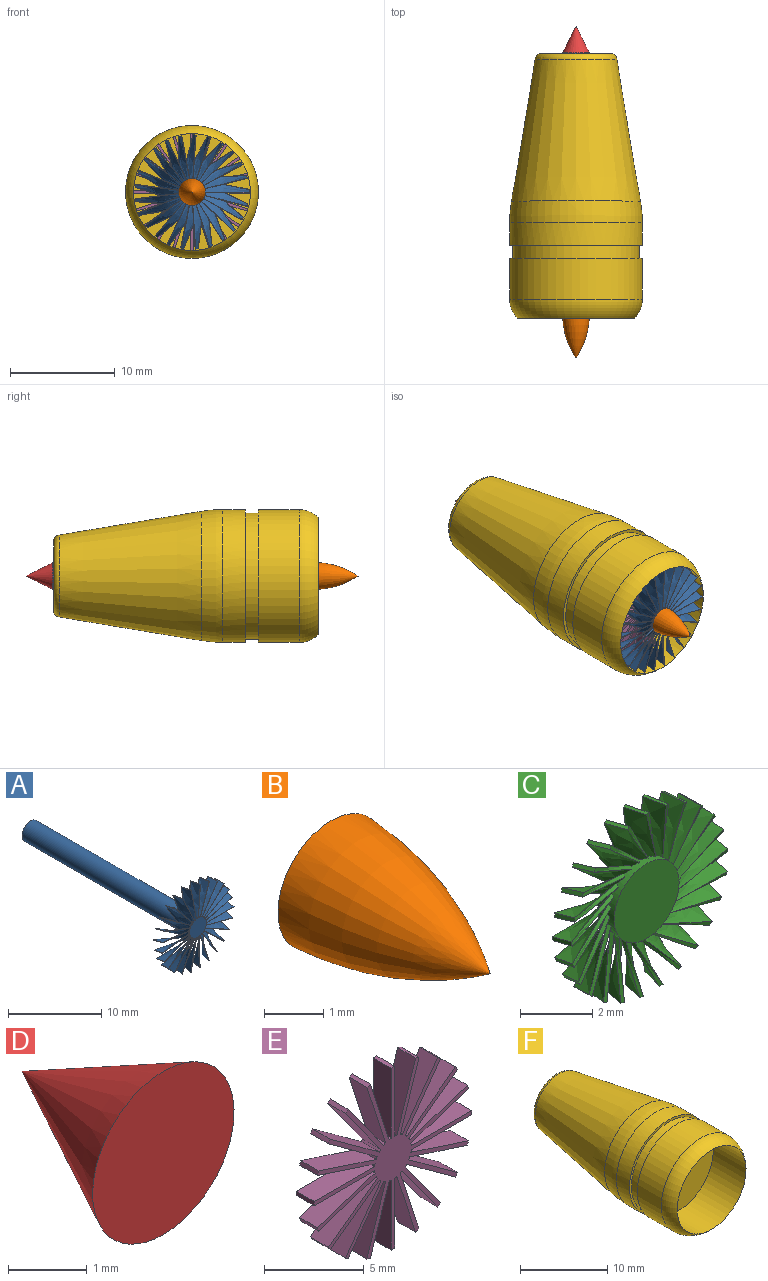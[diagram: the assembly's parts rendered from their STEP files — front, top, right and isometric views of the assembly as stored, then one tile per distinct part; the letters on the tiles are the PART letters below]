
ASSEMBLY  parts=6 mates=5
PART A: 155 faces, bbox 10.9x25.4x10.9 mm
  f0: cylinder r=1.27mm len=25.4mm, axis (0,-1,0), area 201.4mm2, adj f1,f2,f3,f4,f5,f7,f8,f9
  f1: cylinder r=1.27mm len=0.24mm, axis (0,-1,0), area 0mm2, adj f0,f4,f63
  f2: cylinder r=1.27mm len=0.54mm, axis (0,-1,0), area 0.1mm2, adj f0,f4,f57,f61,f62
  f3: plane 2.54x2.54mm, normal (0,1,0), area 5.1mm2, adj f0
  f4: plane 2.54x2.54mm, normal (0,-1,0), area 5.1mm2, adj f0,f1,f2
  f5: plane 0.37x0.23mm, normal (-1,0,0), area 0mm2, adj f0,f7,f9,f10
  f6: plane 1.26x0.3mm, normal (1,0,0), area 0.1mm2, adj f7,f8,f9,f10
  f7: bspline ~4.45x1.25mm, area 5.2mm2, adj f0,f5,f6,f8,f10
  f8: bspline ~4.45x0.05mm, area 0.2mm2, adj f0,f6,f7,f9
  f9: bspline ~4.45x1.25mm, area 5.2mm2, adj f0,f5,f6,f8,f10
  f10: bspline ~4.45x0.94mm, area 0.2mm2, adj f5,f6,f7,f9
  f11: plane 1.26x0.26mm, normal (0.88,0,0.48), area 0.1mm2, adj f12,f13,f14,f15
  f12: bspline ~4.35x1.38mm, area 0.2mm2, adj f11,f13,f15,f16
  f13: bspline ~4.46x2.34mm, area 5.2mm2, adj f0,f11,f12,f14,f16
  f14: bspline ~3.92x2.16mm, area 0.2mm2, adj f0,f11,f13,f15
  f15: bspline ~4.44x2.36mm, area 5.2mm2, adj f0,f11,f12,f14,f16
  f16: plane 0.33x0.23mm, normal (-0.88,0,-0.48), area 0mm2, adj f0,f12,f13,f15
  f17: plane 1.26x0.22mm, normal (0.73,0,0.68), area 0.1mm2, adj f18,f19,f20,f21
  f18: bspline ~3.88x2.41mm, area 0.2mm2, adj f17,f19,f21,f22
  f19: bspline ~4.04x3.2mm, area 5.2mm2, adj f0,f17,f18,f20,f22
  f20: bspline ~3.09x2.89mm, area 0.2mm2, adj f0,f17,f19,f21
  f21: bspline ~4.02x3.22mm, area 5.2mm2, adj f0,f17,f18,f20,f22
  f22: plane 0.27x0.26mm, normal (-0.73,0,-0.68), area 0mm2, adj f0,f18,f19,f21
  f23: plane 1.26x0.3mm, normal (0.06,0,1), area 0.1mm2, adj f24,f25,f26,f27
  f24: bspline ~4.38x1.21mm, area 0.2mm2, adj f23,f25,f27,f28
  f25: bspline ~4.45x1.44mm, area 5.2mm2, adj f0,f23,f24,f26,f28
  f26: bspline ~4.44x0.33mm, area 0.2mm2, adj f0,f23,f25,f27
  f27: bspline ~4.45x1.41mm, area 5.2mm2, adj f0,f23,f24,f26,f28
  f28: plane 0.37x0.23mm, normal (-0.06,0,-1), area 0mm2, adj f0,f24,f25,f27
  f29: plane 1.26x0.27mm, normal (-0.43,0,0.9), area 0.1mm2, adj f30,f31,f32,f33
  f30: bspline ~4.42x1.11mm, area 0.2mm2, adj f29,f31,f33,f34
  f31: bspline ~4.52x2.09mm, area 5.2mm2, adj f0,f29,f30,f32,f34
  f32: bspline ~4.04x1.91mm, area 0.2mm2, adj f0,f29,f31,f33
  f33: bspline ~4.51x2.12mm, area 5.2mm2, adj f0,f29,f30,f32,f34
  f34: plane 0.34x0.23mm, normal (0.43,0,-0.9), area 0mm2, adj f0,f30,f31,f33
  f35: plane 1.26x0.24mm, normal (-0.81,0,0.59), area 0.1mm2, adj f36,f37,f38,f39
  f36: bspline ~3.37x3.09mm, area 0.2mm2, adj f35,f37,f39,f40
  f37: bspline ~3.73x3.55mm, area 5.2mm2, adj f0,f35,f36,f38,f40
  f38: bspline ~3.61x2.65mm, area 0.2mm2, adj f0,f35,f37,f39
  f39: bspline ~3.74x3.53mm, area 5.2mm2, adj f0,f35,f36,f38,f40
  f40: plane 0.3x0.23mm, normal (0.81,0,-0.59), area 0mm2, adj f0,f36,f37,f39
  f41: plane 1.26x0.3mm, normal (-0.99,0,0.13), area 0.1mm2, adj f42,f43,f44,f45
  f42: bspline ~4.3x1.49mm, area 0.2mm2, adj f41,f43,f45,f46
  f43: bspline ~4.44x1.71mm, area 5.2mm2, adj f0,f41,f42,f44,f46
  f44: bspline ~4.16x0.57mm, area 0.2mm2, adj f0,f41,f43,f45
  f45: bspline ~4.44x1.68mm, area 5.2mm2, adj f0,f41,f42,f44,f46
  f46: plane 0.37x0.23mm, normal (0.99,0,-0.13), area 0mm2, adj f0,f42,f43,f45
  f47: plane 1.26x0.28mm, normal (-0.93,0,-0.37), area 0.1mm2, adj f48,f49,f50,f51
  f48: bspline ~4.48x0.83mm, area 0.2mm2, adj f47,f49,f51,f52
  f49: bspline ~4.56x1.84mm, area 5.2mm2, adj f0,f47,f48,f50,f52
  f50: bspline ~4.15x1.66mm, area 0.2mm2, adj f0,f47,f49,f51
  f51: bspline ~4.55x1.87mm, area 5.2mm2, adj f0,f47,f48,f50,f52
  f52: plane 0.35x0.23mm, normal (0.93,0,0.37), area 0mm2, adj f0,f48,f49,f51
  f53: plane 1.26x0.27mm, normal (-0.43,0,-0.9), area 0.1mm2, adj f54,f55,f56,f57
  f54: bspline ~3.65x2.74mm, area 0.2mm2, adj f53,f55,f57,f58
  f55: bspline ~4.12x2.95mm, area 5.2mm2, adj f0,f53,f54,f56,f58
  f56: bspline ~4.03x1.94mm, area 0.2mm2, adj f0,f53,f55,f57
  f57: bspline ~4.13x2.92mm, area 5.2mm2, adj f0,f2,f53,f54,f56,f58
  f58: plane 0.34x0.23mm, normal (0.43,0,0.9), area 0mm2, adj f0,f54,f55,f57
  f59: plane 1.26x0.29mm, normal (-0.19,0,-0.98), area 0.1mm2, adj f60,f61,f62,f63
  f60: bspline ~4.2x1.75mm, area 0.2mm2, adj f59,f61,f63,f64
  f61: bspline ~4.41x1.98mm, area 5.2mm2, adj f0,f2,f59,f60,f62,f64
  f62: bspline ~4.37x0.88mm, area 0.2mm2, adj f2,f59,f61,f63
  f63: bspline ~4.41x1.95mm, area 5.2mm2, adj f0,f1,f59,f60,f62,f64
  f64: plane 0.37x0.23mm, normal (0.19,0,0.98), area 0mm2, adj f0,f60,f61,f63
  f65: plane 1.26x0.28mm, normal (0.31,0,-0.95), area 0.1mm2, adj f66,f67,f68,f69
  f66: bspline ~4.52x0.69mm, area 0.2mm2, adj f65,f67,f69,f70
  f67: bspline ~4.59x1.58mm, area 5.2mm2, adj f0,f65,f66,f68,f70
  f68: bspline ~4.24x1.4mm, area 0.2mm2, adj f0,f65,f67,f69
  f69: bspline ~4.58x1.61mm, area 5.2mm2, adj f0,f65,f66,f68,f70
  f70: plane 0.36x0.23mm, normal (-0.31,0,0.95), area 0mm2, adj f0,f66,f67,f69
  f71: plane 1.26x0.22mm, normal (0.73,0,-0.68), area 0.1mm2, adj f72,f73,f74,f75
  f72: bspline ~3.73x2.65mm, area 0.2mm2, adj f71,f73,f75,f76
  f73: bspline ~3.89x3.39mm, area 5.2mm2, adj f0,f71,f72,f74,f76
  f74: bspline ~3.26x3.08mm, area 0.2mm2, adj f0,f71,f73,f75
  f75: bspline ~3.87x3.41mm, area 5.2mm2, adj f0,f71,f72,f74,f76
  f76: plane 0.27x0.26mm, normal (-0.73,0,0.68), area 0mm2, adj f0,f72,f73,f75
  f77: plane 1.26x0.29mm, normal (0.97,0,-0.25), area 0.1mm2, adj f78,f79,f80,f81
  f78: bspline ~4.09x2.01mm, area 0.2mm2, adj f77,f79,f81,f82
  f79: bspline ~4.36x2.23mm, area 5.2mm2, adj f0,f77,f78,f80,f82
  f80: bspline ~4.07x1.09mm, area 0.2mm2, adj f0,f77,f79,f81
  f81: bspline ~4.37x2.21mm, area 5.2mm2, adj f0,f77,f78,f80,f82
  f82: plane 0.36x0.23mm, normal (-0.97,0,0.25), area 0mm2, adj f0,f78,f79,f81
  f83: plane 1.26x0.26mm, normal (0.88,0,-0.48), area 0.1mm2, adj f84,f86,f87,f88
  f84: bspline ~3.48x2.96mm, area 0.2mm2, adj f83,f85,f86,f88
  f85: plane 0.33x0.23mm, normal (-0.88,0,0.48), area 0mm2, adj f0,f84,f86,f88
  f86: bspline ~4.02x3.14mm, area 5.2mm2, adj f0,f83,f84,f85,f87
  f87: bspline ~3.91x2.19mm, area 0.2mm2, adj f0,f83,f86,f88
  f88: bspline ~4x3.16mm, area 5.2mm2, adj f0,f83,f84,f85,f87
  f89: plane 1.26x0.25mm, normal (0.54,0,-0.84), area 0.1mm2, adj f90,f92,f93,f94
  f90: bspline ~4.26x1.65mm, area 0.2mm2, adj f89,f91,f92,f94
  f91: plane 0.32x0.23mm, normal (-0.54,0,0.84), area 0mm2, adj f0,f90,f92,f94
  f92: bspline ~4.36x2.59mm, area 5.2mm2, adj f0,f89,f90,f91,f93
  f93: bspline ~3.57x2.27mm, area 0.2mm2, adj f0,f89,f92,f94
  f94: bspline ~4.38x2.57mm, area 5.2mm2, adj f0,f89,f90,f91,f93
  f95: plane 1.26x0.3mm, normal (0.06,0,-1), area 0.1mm2, adj f96,f98,f99,f100
  f96: bspline ~4.5x0.69mm, area 0.2mm2, adj f95,f97,f98,f100
  f97: plane 0.37x0.23mm, normal (-0.06,0,1), area 0mm2, adj f0,f96,f98,f100
  f98: bspline ~4.51x1.25mm, area 5.2mm2, adj f0,f95,f96,f97,f99
  f99: bspline ~4.44x0.3mm, area 0.2mm2, adj f0,f95,f98,f100
  f100: bspline ~4.51x1.25mm, area 5.2mm2, adj f0,f95,f96,f97,f99
  f101: plane 1.26x0.23mm, normal (-0.64,0,-0.77), area 0.1mm2, adj f102,f104,f105,f106
  f102: bspline ~3.56x2.87mm, area 0.2mm2, adj f101,f103,f104,f106
  f103: plane 0.29x0.24mm, normal (0.64,0,0.77), area 0mm2, adj f0,f102,f104,f106
  f104: bspline ~3.71x3.58mm, area 5.2mm2, adj f0,f101,f102,f103,f105
  f105: bspline ~3.25x2.71mm, area 0.2mm2, adj f0,f101,f104,f106
  f106: bspline ~3.73x3.57mm, area 5.2mm2, adj f0,f101,f102,f103,f105
  f107: plane 1.26x0.24mm, normal (-0.81,0,-0.59), area 0.1mm2, adj f108,f110,f111,f112
  f108: bspline ~4.15x1.91mm, area 0.2mm2, adj f107,f109,f110,f112
  f109: plane 0.3x0.23mm, normal (0.81,0,0.59), area 0mm2, adj f0,f108,f110,f112
  f110: bspline ~4.26x2.81mm, area 5.2mm2, adj f0,f107,f108,f109,f111
  f111: bspline ~3.42x2.48mm, area 0.2mm2, adj f0,f107,f110,f112
  f112: bspline ~4.28x2.79mm, area 5.2mm2, adj f0,f107,f108,f109,f111
  f113: plane 1.26x0.3mm, normal (-0.99,0,-0.13), area 0.1mm2, adj f114,f116,f117,f118
  f114: bspline ~4.53x0.69mm, area 0.2mm2, adj f113,f115,f116,f118
  f115: plane 0.37x0.23mm, normal (0.99,0,0.13), area 0mm2, adj f0,f114,f116,f118
  f116: bspline ~4.55x1.25mm, area 5.2mm2, adj f0,f113,f114,f115,f117
  f117: bspline ~4.42x0.58mm, area 0.2mm2, adj f0,f113,f116,f118
  f118: bspline ~4.56x1.25mm, area 5.2mm2, adj f0,f113,f114,f115,f117
  f119: plane 1.26x0.28mm, normal (-0.93,0,0.37), area 0.1mm2, adj f120,f122,f123,f124
  f120: bspline ~3.81x2.51mm, area 0.2mm2, adj f119,f121,f122,f124
  f121: plane 0.35x0.23mm, normal (0.93,0,-0.37), area 0mm2, adj f0,f120,f122,f124
  f122: bspline ~4.22x2.69mm, area 5.2mm2, adj f0,f119,f120,f121,f123
  f123: bspline ~3.91x1.59mm, area 0.2mm2, adj f0,f119,f122,f124
  f124: bspline ~4.21x2.72mm, area 5.2mm2, adj f0,f119,f120,f121,f123
  f125: plane 1.26x0.23mm, normal (-0.64,0,0.77), area 0.1mm2, adj f126,f128,f129,f130
  f126: bspline ~4.02x2.17mm, area 0.2mm2, adj f125,f127,f128,f130
  f127: plane 0.29x0.24mm, normal (0.64,0,-0.77), area 0mm2, adj f0,f126,f128,f130
  f128: bspline ~4.15x3.03mm, area 5.2mm2, adj f0,f125,f126,f127,f129
  f129: bspline ~3.46x2.85mm, area 0.2mm2, adj f0,f125,f128,f130
  f130: bspline ~4.17x3mm, area 5.2mm2, adj f0,f125,f126,f127,f129
  f131: plane 1.26x0.29mm, normal (-0.19,0,0.98), area 0.1mm2, adj f132,f134,f135,f136
  f132: bspline ~4.54x0.69mm, area 0.2mm2, adj f131,f133,f134,f136
  f133: plane 0.37x0.23mm, normal (0.19,0,-0.98), area 0mm2, adj f0,f132,f134,f136
  f134: bspline ~4.58x1.25mm, area 5.2mm2, adj f0,f131,f132,f133,f135
  f135: bspline ~4.13x0.81mm, area 0.2mm2, adj f0,f131,f134,f136
  f136: bspline ~4.58x1.25mm, area 5.2mm2, adj f0,f131,f132,f133,f135
  f137: plane 1.26x0.28mm, normal (0.31,0,0.95), area 0.1mm2, adj f138,f140,f141,f142
  f138: bspline ~3.96x2.26mm, area 0.2mm2, adj f137,f139,f140,f142
  f139: plane 0.36x0.23mm, normal (-0.31,0,-0.95), area 0mm2, adj f0,f138,f140,f142
  f140: bspline ~4.3x2.45mm, area 5.2mm2, adj f0,f137,f138,f139,f141
  f141: bspline ~4.23x1.42mm, area 0.2mm2, adj f0,f137,f140,f142
  f142: bspline ~4.3x2.48mm, area 5.2mm2, adj f0,f137,f138,f139,f141
  f143: plane 1.26x0.25mm, normal (0.54,0,0.84), area 0.1mm2, adj f144,f146,f147,f148
  f144: bspline ~3.29x3.17mm, area 0.2mm2, adj f143,f145,f146,f148
  f145: plane 0.32x0.23mm, normal (-0.54,0,-0.84), area 0mm2, adj f0,f144,f146,f148
  f146: bspline ~3.89x3.34mm, area 5.2mm2, adj f0,f143,f144,f145,f147
  f147: bspline ~3.55x2.29mm, area 0.2mm2, adj f0,f143,f146,f148
  f148: bspline ~3.87x3.36mm, area 5.2mm2, adj f0,f143,f144,f145,f147
  f149: plane 0.36x0.23mm, normal (-0.97,0,-0.25), area 0mm2, adj f0,f151,f153,f154
  f150: plane 1.26x0.29mm, normal (0.97,0,0.25), area 0.1mm2, adj f151,f152,f153,f154
  f151: bspline ~4.59x1.35mm, area 5.2mm2, adj f0,f149,f150,f152,f154
  f152: bspline ~4.32x1.13mm, area 0.2mm2, adj f0,f150,f151,f153
  f153: bspline ~4.59x1.32mm, area 5.2mm2, adj f0,f149,f150,f152,f154
  f154: bspline ~4.54x0.69mm, area 0.2mm2, adj f149,f150,f151,f153
PART B: 2 faces, bbox 2.5x3.8x2.5 mm
  f0: plane 2.54x2.54mm, normal (0,1,0), area 5.1mm2, adj f1
  f1: revolved ~3.81x2.54mm, area 20.7mm2, adj f0
PART C: 153 faces, bbox 6.1x0.8x6.1 mm
  f0: bspline ~2.03x0.12mm, area 0.2mm2, adj f1,f2,f3,f146
  f1: bspline ~2.03x0.75mm, area 1.3mm2, adj f0,f2,f4,f10,f11,f126,f146
  f2: plane 0.77x0.31mm, normal (-1,0,0), area 0.1mm2, adj f0,f1,f3,f4
  f3: bspline ~2.03x0.74mm, area 1.3mm2, adj f0,f2,f4,f6,f149
  f4: bspline ~2.03x0.62mm, area 0.2mm2, adj f1,f2,f3,f6,f126
  f5: bspline ~1.75x0.51mm, area 0.2mm2, adj f6,f122,f123,f149
  f6: bspline ~2.04x0.74mm, area 1.3mm2, adj f3,f4,f5,f122,f124,f126,f149
  f7: bspline ~1.98x0.62mm, area 0.2mm2, adj f8,f9,f10,f143
  f8: bspline ~2x1.23mm, area 1.3mm2, adj f7,f9,f11,f15,f16,f126,f143
  f9: plane 0.77x0.3mm, normal (-0.97,0,-0.25), area 0.1mm2, adj f7,f8,f10,f11
  f10: bspline ~1.92x1.12mm, area 1.3mm2, adj f1,f7,f9,f11,f146
  f11: bspline ~1.86x1.11mm, area 0.2mm2, adj f1,f8,f9,f10,f126
  f12: bspline ~1.81x1.09mm, area 0.2mm2, adj f13,f14,f15,f140
  f13: bspline ~1.84x1.63mm, area 1.3mm2, adj f12,f14,f16,f20,f21,f126,f140
  f14: plane 0.77x0.27mm, normal (-0.88,0,-0.48), area 0.1mm2, adj f12,f13,f15,f16
  f15: bspline ~1.87x1.58mm, area 1.3mm2, adj f8,f12,f14,f16,f143
  f16: bspline ~1.57x1.52mm, area 0.2mm2, adj f8,f13,f14,f15,f126
  f17: bspline ~1.34x1.31mm, area 0.2mm2, adj f18,f19,f20,f137
  f18: bspline ~1.94x1.56mm, area 1.3mm2, adj f17,f19,f21,f25,f26,f126,f137
  f19: plane 0.77x0.22mm, normal (-0.73,0,-0.68), area 0.1mm2, adj f17,f18,f20,f21
  f20: bspline ~1.89x1.61mm, area 1.3mm2, adj f13,f17,f19,f21,f140
  f21: bspline ~1.78x1.14mm, area 0.2mm2, adj f13,f18,f19,f20,f126
  f22: bspline ~1.78x1.14mm, area 0.2mm2, adj f23,f24,f25,f134
  f23: bspline ~2.12x1.19mm, area 1.3mm2, adj f22,f24,f26,f30,f31,f126,f134
  f24: plane 0.77x0.26mm, normal (-0.54,0,-0.84), area 0.1mm2, adj f22,f23,f25,f26
  f25: bspline ~2.08x1.25mm, area 1.3mm2, adj f18,f22,f24,f26,f137
  f26: bspline ~2.05x0.72mm, area 0.2mm2, adj f18,f23,f24,f25,f126
  f27: bspline ~1.97x0.68mm, area 0.2mm2, adj f28,f29,f30,f131
  f28: bspline ~2.16x0.74mm, area 1.3mm2, adj f27,f29,f31,f35,f36,f126,f131
  f29: plane 0.77x0.29mm, normal (-0.31,0,-0.95), area 0.1mm2, adj f27,f28,f30,f31
  f30: bspline ~2.14x0.8mm, area 1.3mm2, adj f23,f27,f29,f31,f134
  f31: bspline ~2.12x0.43mm, area 0.2mm2, adj f23,f28,f29,f30,f126
  f32: bspline ~1.78x0.18mm, area 0.2mm2, adj f33,f34,f35,f128
  f33: bspline ~1.97x0.74mm, area 1.3mm2, adj f32,f34,f36,f40,f41,f126,f128
  f34: plane 0.77x0.31mm, normal (-0.06,0,-1), area 0.1mm2, adj f32,f33,f35,f36
  f35: bspline ~2.07x0.74mm, area 1.3mm2, adj f28,f32,f34,f36,f131
  f36: bspline ~2.07x0.49mm, area 0.2mm2, adj f28,f33,f34,f35,f126
  f37: bspline ~2.01x0.5mm, area 0.2mm2, adj f38,f39,f40,f127
  f38: bspline ~2.02x1.12mm, area 1.3mm2, adj f37,f39,f41,f45,f46,f126,f127
  f39: plane 0.77x0.3mm, normal (0.19,0,-0.98), area 0.1mm2, adj f37,f38,f40,f41
  f40: bspline ~2.03x1.05mm, area 1.3mm2, adj f33,f37,f39,f41,f128
  f41: bspline ~1.91x0.99mm, area 0.2mm2, adj f33,f38,f39,f40,f126
  f42: bspline ~1.86x0.98mm, area 0.2mm2, adj f43,f44,f45,f129
  f43: bspline ~1.89x1.54mm, area 1.3mm2, adj f42,f44,f46,f50,f51,f126,f129
  f44: plane 0.77x0.28mm, normal (0.43,0,-0.9), area 0.1mm2, adj f42,f43,f45,f46
  f45: bspline ~1.92x1.48mm, area 1.3mm2, adj f38,f42,f44,f46,f127
  f46: bspline ~1.65x1.43mm, area 0.2mm2, adj f38,f43,f44,f45,f126
  f47: bspline ~1.6x1.39mm, area 0.2mm2, adj f48,f49,f50,f130
  f48: bspline ~1.87x1.64mm, area 1.3mm2, adj f47,f49,f51,f55,f56,f126,f130
  f49: plane 0.77x0.24mm, normal (0.64,0,-0.77), area 0.1mm2, adj f47,f48,f50,f51
  f50: bspline ~1.82x1.68mm, area 1.3mm2, adj f43,f47,f49,f51,f129
  f51: bspline ~1.77x1.29mm, area 0.2mm2, adj f43,f48,f49,f50,f126
  f52: bspline ~1.51x1.1mm, area 0.2mm2, adj f53,f54,f55,f132
  f53: bspline ~2.08x1.29mm, area 1.3mm2, adj f52,f54,f56,f60,f61,f126,f132
  f54: plane 0.77x0.25mm, normal (0.81,0,-0.59), area 0.1mm2, adj f52,f53,f55,f56
  f55: bspline ~1.95x1.29mm, area 1.3mm2, adj f48,f52,f54,f56,f130
  f56: bspline ~2.01x0.84mm, area 0.2mm2, adj f48,f53,f54,f55,f126
  f57: bspline ~1.93x0.8mm, area 0.2mm2, adj f58,f59,f60,f133
  f58: bspline ~2.16x0.86mm, area 1.3mm2, adj f57,f59,f61,f65,f66,f126,f133
  f59: plane 0.77x0.29mm, normal (0.93,0,-0.37), area 0.1mm2, adj f57,f58,f60,f61
  f60: bspline ~2.14x0.92mm, area 1.3mm2, adj f53,f57,f59,f61,f132
  f61: bspline ~2.12x0.43mm, area 0.2mm2, adj f53,f58,f59,f60,f126
  f62: bspline ~2.03x0.31mm, area 0.2mm2, adj f63,f64,f65,f135
  f63: bspline ~2.11x0.74mm, area 1.3mm2, adj f62,f64,f66,f70,f71,f126,f135
  f64: plane 0.77x0.31mm, normal (0.99,0,-0.13), area 0.1mm2, adj f62,f63,f65,f66
  f65: bspline ~2.1x0.74mm, area 1.3mm2, adj f58,f62,f64,f66,f133
  f66: bspline ~2.09x0.43mm, area 0.2mm2, adj f58,f63,f64,f65,f126
  f67: bspline ~2.02x0.38mm, area 0.2mm2, adj f68,f69,f70,f136
  f68: bspline ~2.03x1mm, area 1.3mm2, adj f67,f69,f71,f75,f76,f126,f136
  f69: plane 0.77x0.31mm, normal (0.99,0,0.13), area 0.1mm2, adj f67,f68,f70,f71
  f70: bspline ~2.04x0.93mm, area 1.3mm2, adj f63,f67,f69,f71,f135
  f71: bspline ~1.96x0.87mm, area 0.2mm2, adj f63,f68,f69,f70,f126
  f72: bspline ~1.91x0.86mm, area 0.2mm2, adj f73,f74,f75,f138
  f73: bspline ~1.93x1.44mm, area 1.3mm2, adj f72,f74,f76,f80,f81,f126,f138
  f74: plane 0.77x0.29mm, normal (0.93,0,0.37), area 0.1mm2, adj f72,f73,f75,f76
  f75: bspline ~1.86x1.32mm, area 1.3mm2, adj f68,f72,f74,f76,f136
  f76: bspline ~1.67x1.28mm, area 0.2mm2, adj f68,f73,f74,f75,f126
  f77: bspline ~1.68x1.29mm, area 0.2mm2, adj f78,f79,f80,f139
  f78: bspline ~1.8x1.71mm, area 1.3mm2, adj f77,f79,f81,f85,f86,f126,f139
  f79: plane 0.77x0.25mm, normal (0.81,0,0.59), area 0.1mm2, adj f77,f78,f80,f81
  f80: bspline ~1.75x1.75mm, area 1.3mm2, adj f73,f77,f79,f81,f138
  f81: bspline ~1.7x1.39mm, area 0.2mm2, adj f73,f78,f79,f80,f126
  f82: bspline ~1.45x1.18mm, area 0.2mm2, adj f83,f84,f85,f141
  f83: bspline ~2.04x1.39mm, area 1.3mm2, adj f82,f84,f86,f90,f91,f126,f141
  f84: plane 0.77x0.24mm, normal (0.64,0,0.77), area 0.1mm2, adj f82,f83,f85,f86
  f85: bspline ~2x1.44mm, area 1.3mm2, adj f78,f82,f84,f86,f139
  f86: bspline ~1.96x0.96mm, area 0.2mm2, adj f78,f83,f84,f85,f126
  f87: bspline ~1.66x0.82mm, area 0.2mm2, adj f88,f89,f90,f142
  f88: bspline ~2.05x0.93mm, area 1.3mm2, adj f87,f89,f91,f95,f96,f126,f142
  f89: plane 0.77x0.28mm, normal (0.43,0,0.9), area 0.1mm2, adj f87,f88,f90,f91
  f90: bspline ~2.13x1.03mm, area 1.3mm2, adj f83,f87,f89,f91,f141
  f91: bspline ~2.1x0.47mm, area 0.2mm2, adj f83,f88,f89,f90,f126
  f92: bspline ~2.02x0.44mm, area 0.2mm2, adj f93,f94,f95,f144
  f93: bspline ~2.14x0.74mm, area 1.3mm2, adj f92,f94,f96,f100,f101,f126,f144
  f94: plane 0.77x0.3mm, normal (0.19,0,0.98), area 0.1mm2, adj f92,f93,f95,f96
  f95: bspline ~2.12x0.74mm, area 1.3mm2, adj f88,f92,f94,f96,f142
  f96: bspline ~2.04x0.42mm, area 0.2mm2, adj f88,f93,f94,f95,f126
  f97: bspline ~2.03x0.25mm, area 0.2mm2, adj f98,f99,f100,f145
  f98: bspline ~2.04x0.87mm, area 1.3mm2, adj f97,f99,f101,f105,f106,f126,f145
  f99: plane 0.77x0.31mm, normal (-0.06,0,1), area 0.1mm2, adj f97,f98,f100,f101
  f100: bspline ~1.94x0.78mm, area 1.3mm2, adj f93,f97,f99,f101,f144
  f101: bspline ~2x0.75mm, area 0.2mm2, adj f93,f98,f99,f100,f126
  f102: bspline ~1.71x0.67mm, area 0.2mm2, adj f103,f104,f105,f147
  f103: bspline ~1.97x1.34mm, area 1.3mm2, adj f102,f104,f106,f110,f111,f126,f147
  f104: plane 0.77x0.29mm, normal (-0.31,0,0.95), area 0.1mm2, adj f102,f103,f105,f106
  f105: bspline ~1.99x1.28mm, area 1.3mm2, adj f98,f102,f104,f106,f145
  f106: bspline ~1.74x1.18mm, area 0.2mm2, adj f98,f103,f104,f105,f126
  f107: bspline ~1.75x1.19mm, area 0.2mm2, adj f108,f109,f110,f148
  f108: bspline ~1.78x1.72mm, area 1.3mm2, adj f107,f109,f111,f115,f116,f126,f148
  f109: plane 0.77x0.26mm, normal (-0.54,0,0.84), area 0.1mm2, adj f107,f108,f110,f111
  f110: bspline ~1.81x1.66mm, area 1.3mm2, adj f103,f107,f109,f111,f147
  f111: bspline ~1.61x1.48mm, area 0.2mm2, adj f103,f108,f109,f110,f126
  f112: bspline ~1.57x1.43mm, area 0.2mm2, adj f113,f114,f115,f150
  f113: bspline ~1.99x1.48mm, area 1.3mm2, adj f112,f114,f116,f120,f121,f126,f150
  f114: plane 0.77x0.22mm, normal (-0.73,0,0.68), area 0.1mm2, adj f112,f113,f115,f116
  f115: bspline ~1.95x1.53mm, area 1.3mm2, adj f108,f112,f114,f116,f148
  f116: bspline ~1.91x1.07mm, area 0.2mm2, adj f108,f113,f114,f115,f126
  f117: bspline ~1.84x1.03mm, area 0.2mm2, adj f118,f119,f120,f151
  f118: bspline ~2.14x1.08mm, area 1.3mm2, adj f117,f119,f121,f123,f124,f126,f151
  f119: plane 0.77x0.27mm, normal (-0.88,0,0.48), area 0.1mm2, adj f117,f118,f120,f121
  f120: bspline ~2.11x1.14mm, area 1.3mm2, adj f113,f117,f119,f121,f150
  f121: bspline ~2.08x0.59mm, area 0.2mm2, adj f113,f118,f119,f120,f126
  f122: plane 0.77x0.3mm, normal (-0.97,0,0.25), area 0.1mm2, adj f5,f6,f123,f124
  f123: bspline ~2.14x0.74mm, area 1.3mm2, adj f5,f118,f122,f124,f151
  f124: bspline ~2.12x0.43mm, area 0.2mm2, adj f6,f118,f122,f123,f126
  f125: plane 2.54x2.54mm, normal (0,-1,0), area 5.1mm2, adj f126
  f126: cylinder r=1.27mm len=2.54mm, axis (0,1,0), area 1.7mm2, adj f1,f4,f6,f8,f11,f13,f16,f18
  f127: cylinder r=1.27mm len=0.61mm, axis (0,1,0), area 0mm2, adj f37,f38,f45,f152
  f128: cylinder r=1.27mm len=0.63mm, axis (0,1,0), area 0mm2, adj f32,f33,f40,f152
  f129: cylinder r=1.27mm len=0.57mm, axis (0,1,0), area 0mm2, adj f42,f43,f50,f152
  f130: cylinder r=1.27mm len=0.48mm, axis (0,1,0), area 0mm2, adj f47,f48,f55,f152
  f131: cylinder r=1.27mm len=0.6mm, axis (0,1,0), area 0mm2, adj f27,f28,f35,f152
  f132: cylinder r=1.27mm len=0.51mm, axis (0,1,0), area 0mm2, adj f52,f53,f60,f152
  f133: cylinder r=1.27mm len=0.58mm, axis (0,1,0), area 0mm2, adj f57,f58,f65,f152
  f134: cylinder r=1.27mm len=0.53mm, axis (0,1,0), area 0mm2, adj f22,f23,f30,f152
  f135: cylinder r=1.27mm len=0.62mm, axis (0,1,0), area 0mm2, adj f62,f63,f70,f152
  f136: cylinder r=1.27mm len=0.62mm, axis (0,1,0), area 0mm2, adj f67,f68,f75,f152
  f137: cylinder r=1.27mm len=0.46mm, axis (0,1,0), area 0mm2, adj f17,f18,f25,f152
  f138: cylinder r=1.27mm len=0.58mm, axis (0,1,0), area 0mm2, adj f72,f73,f80,f152
  f139: cylinder r=1.27mm len=0.51mm, axis (0,1,0), area 0mm2, adj f77,f78,f85,f152
  f140: cylinder r=1.27mm len=0.55mm, axis (0,1,0), area 0mm2, adj f12,f13,f20,f152
  f141: cylinder r=1.27mm len=0.48mm, axis (0,1,0), area 0mm2, adj f82,f83,f90,f152
  f142: cylinder r=1.27mm len=0.57mm, axis (0,1,0), area 0mm2, adj f87,f88,f95,f152
  f143: cylinder r=1.27mm len=0.61mm, axis (0,1,0), area 0mm2, adj f7,f8,f15,f152
  f144: cylinder r=1.27mm len=0.62mm, axis (0,1,0), area 0mm2, adj f92,f93,f100,f152
  f145: cylinder r=1.27mm len=0.63mm, axis (0,1,0), area 0mm2, adj f97,f98,f105,f152
  f146: cylinder r=1.27mm len=0.63mm, axis (0,1,0), area 0mm2, adj f0,f1,f10,f152
  f147: cylinder r=1.27mm len=0.6mm, axis (0,1,0), area 0mm2, adj f102,f103,f110,f152
  f148: cylinder r=1.27mm len=0.53mm, axis (0,1,0), area 0mm2, adj f107,f108,f115,f152
  f149: cylinder r=1.27mm len=0.61mm, axis (0,1,0), area 0mm2, adj f3,f5,f6,f152
  f150: cylinder r=1.27mm len=0.46mm, axis (0,1,0), area 0mm2, adj f112,f113,f120,f152
  f151: cylinder r=1.27mm len=0.55mm, axis (0,1,0), area 0mm2, adj f117,f118,f123,f152
  f152: plane 2.54x2.54mm, normal (0,1,0), area 5.1mm2, adj f127,f128,f129,f130,f131,f132,f133,f134
PART D: 2 faces, bbox 2.5x2.5x2.5 mm
  f0: plane 2.54x2.54mm, normal (0,-1,0), area 5.1mm2, adj f1
  f1: cone r=1.27mm half-angle=26.6deg, axis (0,-1,0), area 11.3mm2, adj f0
PART E: 82 faces, bbox 11.2x1.3x11.2 mm
  f0: plane 11.18x11.18mm, normal (0,-1,0), area 27.1mm2, adj f1,f2,f3,f5,f6,f7,f8,f9
  f1: cylinder r=5.59mm len=1.27mm, axis (0,-1,0), area 0.3mm2, adj f0,f2,f3,f4
  f2: plane 4.29x1.27mm, normal (0,0,1), area 5.4mm2, adj f0,f1,f4,f5
  f3: plane 4.29x1.27mm, normal (0,0,-1), area 5.4mm2, adj f0,f1,f4,f6
  f4: plane 11.18x11.18mm, normal (0,1,0), area 27.1mm2, adj f1,f2,f3,f5,f6,f7,f8,f9
  f5: cylinder r=1.3mm len=1.27mm, axis (0,-1,0), area 0.2mm2, adj f0,f2,f4,f9
  f6: cylinder r=1.3mm len=1.27mm, axis (0,-1,0), area 0.2mm2, adj f0,f3,f4,f80
  f7: cylinder r=5.59mm len=1.27mm, axis (0,-1,0), area 0.3mm2, adj f0,f4,f8,f9
  f8: plane 4.08x1.33mm, normal (-0.31,0,0.95), area 5.4mm2, adj f0,f4,f7,f10
  f9: plane 4.08x1.33mm, normal (0.31,0,-0.95), area 5.4mm2, adj f0,f4,f5,f7
  f10: cylinder r=1.3mm len=1.27mm, axis (0,-1,0), area 0.2mm2, adj f0,f4,f8,f13
  f11: cylinder r=5.59mm len=1.27mm, axis (0,-1,0), area 0.3mm2, adj f0,f4,f12,f13
  f12: plane 3.47x2.52mm, normal (-0.59,0,0.81), area 5.4mm2, adj f0,f4,f11,f14
  f13: plane 3.47x2.52mm, normal (0.59,0,-0.81), area 5.4mm2, adj f0,f4,f10,f11
  f14: cylinder r=1.3mm len=1.27mm, axis (0,-1,0), area 0.2mm2, adj f0,f4,f12,f17
  f15: cylinder r=5.59mm len=1.27mm, axis (0,-1,0), area 0.3mm2, adj f0,f4,f16,f17
  f16: plane 3.47x2.52mm, normal (-0.81,0,0.59), area 5.4mm2, adj f0,f4,f15,f18
  f17: plane 3.47x2.52mm, normal (0.81,0,-0.59), area 5.4mm2, adj f0,f4,f14,f15
  f18: cylinder r=1.3mm len=1.27mm, axis (0,-1,0), area 0.2mm2, adj f0,f4,f16,f21
  f19: cylinder r=5.59mm len=1.27mm, axis (0,-1,0), area 0.3mm2, adj f0,f4,f20,f21
  f20: plane 4.08x1.33mm, normal (-0.95,0,0.31), area 5.4mm2, adj f0,f4,f19,f22
  f21: plane 4.08x1.33mm, normal (0.95,0,-0.31), area 5.4mm2, adj f0,f4,f18,f19
  f22: cylinder r=1.3mm len=1.27mm, axis (0,-1,0), area 0.2mm2, adj f0,f4,f20,f25
  f23: cylinder r=5.59mm len=1.27mm, axis (0,-1,0), area 0.3mm2, adj f0,f4,f24,f25
  f24: plane 4.29x1.27mm, normal (-1,0,0), area 5.4mm2, adj f0,f4,f23,f26
  f25: plane 4.29x1.27mm, normal (1,0,0), area 5.4mm2, adj f0,f4,f22,f23
  f26: cylinder r=1.3mm len=1.27mm, axis (0,-1,0), area 0.2mm2, adj f0,f4,f24,f29
  f27: cylinder r=5.59mm len=1.27mm, axis (0,-1,0), area 0.3mm2, adj f0,f4,f28,f29
  f28: plane 4.08x1.33mm, normal (-0.95,0,-0.31), area 5.4mm2, adj f0,f4,f27,f30
  f29: plane 4.08x1.33mm, normal (0.95,0,0.31), area 5.4mm2, adj f0,f4,f26,f27
  f30: cylinder r=1.3mm len=1.27mm, axis (0,-1,0), area 0.2mm2, adj f0,f4,f28,f33
  f31: cylinder r=5.59mm len=1.27mm, axis (0,-1,0), area 0.3mm2, adj f0,f4,f32,f33
  f32: plane 3.47x2.52mm, normal (-0.81,0,-0.59), area 5.4mm2, adj f0,f4,f31,f34
  f33: plane 3.47x2.52mm, normal (0.81,0,0.59), area 5.4mm2, adj f0,f4,f30,f31
  f34: cylinder r=1.3mm len=1.27mm, axis (0,-1,0), area 0.2mm2, adj f0,f4,f32,f37
  f35: cylinder r=5.59mm len=1.27mm, axis (0,-1,0), area 0.3mm2, adj f0,f4,f36,f37
  f36: plane 3.47x2.52mm, normal (-0.59,0,-0.81), area 5.4mm2, adj f0,f4,f35,f38
  f37: plane 3.47x2.52mm, normal (0.59,0,0.81), area 5.4mm2, adj f0,f4,f34,f35
  f38: cylinder r=1.3mm len=1.27mm, axis (0,-1,0), area 0.2mm2, adj f0,f4,f36,f41
  f39: cylinder r=5.59mm len=1.27mm, axis (0,-1,0), area 0.3mm2, adj f0,f4,f40,f41
  f40: plane 4.08x1.33mm, normal (-0.31,0,-0.95), area 5.4mm2, adj f0,f4,f39,f42
  f41: plane 4.08x1.33mm, normal (0.31,0,0.95), area 5.4mm2, adj f0,f4,f38,f39
  f42: cylinder r=1.3mm len=1.27mm, axis (0,-1,0), area 0.2mm2, adj f0,f4,f40,f45
  f43: cylinder r=5.59mm len=1.27mm, axis (0,-1,0), area 0.3mm2, adj f0,f4,f44,f45
  f44: plane 4.29x1.27mm, normal (0,0,-1), area 5.4mm2, adj f0,f4,f43,f46
  f45: plane 4.29x1.27mm, normal (0,0,1), area 5.4mm2, adj f0,f4,f42,f43
  f46: cylinder r=1.3mm len=1.27mm, axis (0,-1,0), area 0.2mm2, adj f0,f4,f44,f49
  f47: cylinder r=5.59mm len=1.27mm, axis (0,-1,0), area 0.3mm2, adj f0,f4,f48,f49
  f48: plane 4.08x1.33mm, normal (0.31,0,-0.95), area 5.4mm2, adj f0,f4,f47,f50
  f49: plane 4.08x1.33mm, normal (-0.31,0,0.95), area 5.4mm2, adj f0,f4,f46,f47
  f50: cylinder r=1.3mm len=1.27mm, axis (0,-1,0), area 0.2mm2, adj f0,f4,f48,f58
  f51: cylinder r=5.59mm len=1.27mm, axis (0,-1,0), area 0.3mm2, adj f0,f4,f52,f53
  f52: plane 3.47x2.52mm, normal (0.81,0,-0.59), area 5.4mm2, adj f0,f4,f51,f54
  f53: plane 3.47x2.52mm, normal (-0.81,0,0.59), area 5.4mm2, adj f0,f4,f51,f55
  f54: cylinder r=1.3mm len=1.27mm, axis (0,-1,0), area 0.2mm2, adj f0,f4,f52,f61
  f55: cylinder r=1.3mm len=1.27mm, axis (0,-1,0), area 0.2mm2, adj f0,f4,f53,f57
  f56: cylinder r=5.59mm len=1.27mm, axis (0,-1,0), area 0.3mm2, adj f0,f4,f57,f58
  f57: plane 3.47x2.52mm, normal (0.59,0,-0.81), area 5.4mm2, adj f0,f4,f55,f56
  f58: plane 3.47x2.52mm, normal (-0.59,0,0.81), area 5.4mm2, adj f0,f4,f50,f56
  f59: cylinder r=5.59mm len=1.27mm, axis (0,-1,0), area 0.3mm2, adj f0,f4,f60,f61
  f60: plane 4.08x1.33mm, normal (0.95,0,-0.31), area 5.4mm2, adj f0,f4,f59,f62
  f61: plane 4.08x1.33mm, normal (-0.95,0,0.31), area 5.4mm2, adj f0,f4,f54,f59
  f62: cylinder r=1.3mm len=1.27mm, axis (0,-1,0), area 0.2mm2, adj f0,f4,f60,f65
  f63: cylinder r=5.59mm len=1.27mm, axis (0,-1,0), area 0.3mm2, adj f0,f4,f64,f65
  f64: plane 4.29x1.27mm, normal (1,0,0), area 5.4mm2, adj f0,f4,f63,f66
  f65: plane 4.29x1.27mm, normal (-1,0,0), area 5.4mm2, adj f0,f4,f62,f63
  f66: cylinder r=1.3mm len=1.27mm, axis (0,-1,0), area 0.2mm2, adj f0,f4,f64,f69
  f67: cylinder r=5.59mm len=1.27mm, axis (0,-1,0), area 0.3mm2, adj f0,f4,f68,f69
  f68: plane 4.08x1.33mm, normal (0.95,0,0.31), area 5.4mm2, adj f0,f4,f67,f70
  f69: plane 4.08x1.33mm, normal (-0.95,0,-0.31), area 5.4mm2, adj f0,f4,f66,f67
  f70: cylinder r=1.3mm len=1.27mm, axis (0,-1,0), area 0.2mm2, adj f0,f4,f68,f73
  f71: cylinder r=5.59mm len=1.27mm, axis (0,-1,0), area 0.3mm2, adj f0,f4,f72,f73
  f72: plane 3.47x2.52mm, normal (0.81,0,0.59), area 5.4mm2, adj f0,f4,f71,f74
  f73: plane 3.47x2.52mm, normal (-0.81,0,-0.59), area 5.4mm2, adj f0,f4,f70,f71
  f74: cylinder r=1.3mm len=1.27mm, axis (0,-1,0), area 0.2mm2, adj f0,f4,f72,f77
  f75: cylinder r=5.59mm len=1.27mm, axis (0,-1,0), area 0.3mm2, adj f0,f4,f76,f77
  f76: plane 3.47x2.52mm, normal (0.59,0,0.81), area 5.4mm2, adj f0,f4,f75,f78
  f77: plane 3.47x2.52mm, normal (-0.59,0,-0.81), area 5.4mm2, adj f0,f4,f74,f75
  f78: cylinder r=1.3mm len=1.27mm, axis (0,-1,0), area 0.2mm2, adj f0,f4,f76,f81
  f79: cylinder r=5.59mm len=1.27mm, axis (0,-1,0), area 0.3mm2, adj f0,f4,f80,f81
  f80: plane 4.08x1.33mm, normal (0.31,0,0.95), area 5.4mm2, adj f0,f4,f6,f79
  f81: plane 4.08x1.33mm, normal (-0.31,0,-0.95), area 5.4mm2, adj f0,f4,f78,f79
PART F: 18 faces, bbox 13.7x26x13.7 mm
  f0: cylinder r=6.35mm len=12.7mm, axis (0,-1,0), area 155.6mm2, adj f7,f17
  f1: cylinder r=5.59mm len=11.18mm, axis (0,-1,0), area 98.1mm2, adj f2,f11
  f2: plane 11.41x11.41mm, normal (0,1,0), area 4.2mm2, adj f1,f5
  f3: cylinder r=6.35mm len=12.7mm, axis (0,-1,0), area 84.7mm2, adj f9,f16
  f4: cylinder r=5.59mm len=11.18mm, axis (0,-1,0), area 187.3mm2, adj f7,f10
  f5: cone r=5.72mm half-angle=9.5deg, axis (0,-1,0), area 428.5mm2, adj f2,f8
  f6: cone r=6.35mm half-angle=9.5deg, axis (0,-1,0), area 436.4mm2, adj f8,f9
  f7: torus R=3.81mm, axis (0,-1,0), area 77.3mm2, adj f0,f4
  f8: torus R=3.29mm, axis (0,-1,0), area 22.7mm2, adj f5,f6
  f9: revolved ~12.7x12.7mm, area 165.8mm2, adj f3,f6
  f10: plane 11.18x11.18mm, normal (0,-1,0), area 86.7mm2, adj f4,f12
  f11: plane 11.18x11.18mm, normal (0,1,0), area 79.8mm2, adj f1,f13
  f12: cylinder r=1.91mm len=18.03mm, axis (0,1,0), area 215.9mm2, adj f10,f14
  f13: cylinder r=2.41mm len=16mm, axis (0,-1,0), area 242.6mm2, adj f11,f14
  f14: plane 4.83x4.83mm, normal (0,1,0), area 6.9mm2, adj f12,f13
  f15: cylinder r=6.03mm len=12.07mm, axis (0,-1,0), area 48.1mm2, adj f16,f17
  f16: plane 12.7x12.7mm, normal (0,-1,0), area 12.4mm2, adj f3,f15
  f17: plane 12.7x12.7mm, normal (0,1,0), area 12.4mm2, adj f0,f15
PLACE A t=(0.69,-7.26,7.48)mm
PLACE B t=(0.69,-7.26,7.48)mm
PLACE C t=(0.69,-6.73,7.48)mm
PLACE D t=(0.69,-7.26,7.48)mm
PLACE E t=(0.69,-7.26,7.48)mm
PLACE F t=(0.69,-7.26,7.48)mm
MATE planar C.f126 <-> F.f0  axis (0,-1,0) through (0.69,17.02,7.48)mm
MATE fastened B.f0 <-> A.f0  axis (0,1,0) through (0.69,-7.26,7.48)mm
MATE planar A.f0 <-> F.f0  axis (0,-1,0) through (0.69,-7.26,7.48)mm
MATE fastened D.f1 <-> A.f0  axis (0,-1,0) through (0.69,18.14,7.48)mm
MATE planar E.f43 <-> F.f0  axis (0,-1,0) through (0.69,-4.72,7.48)mm
